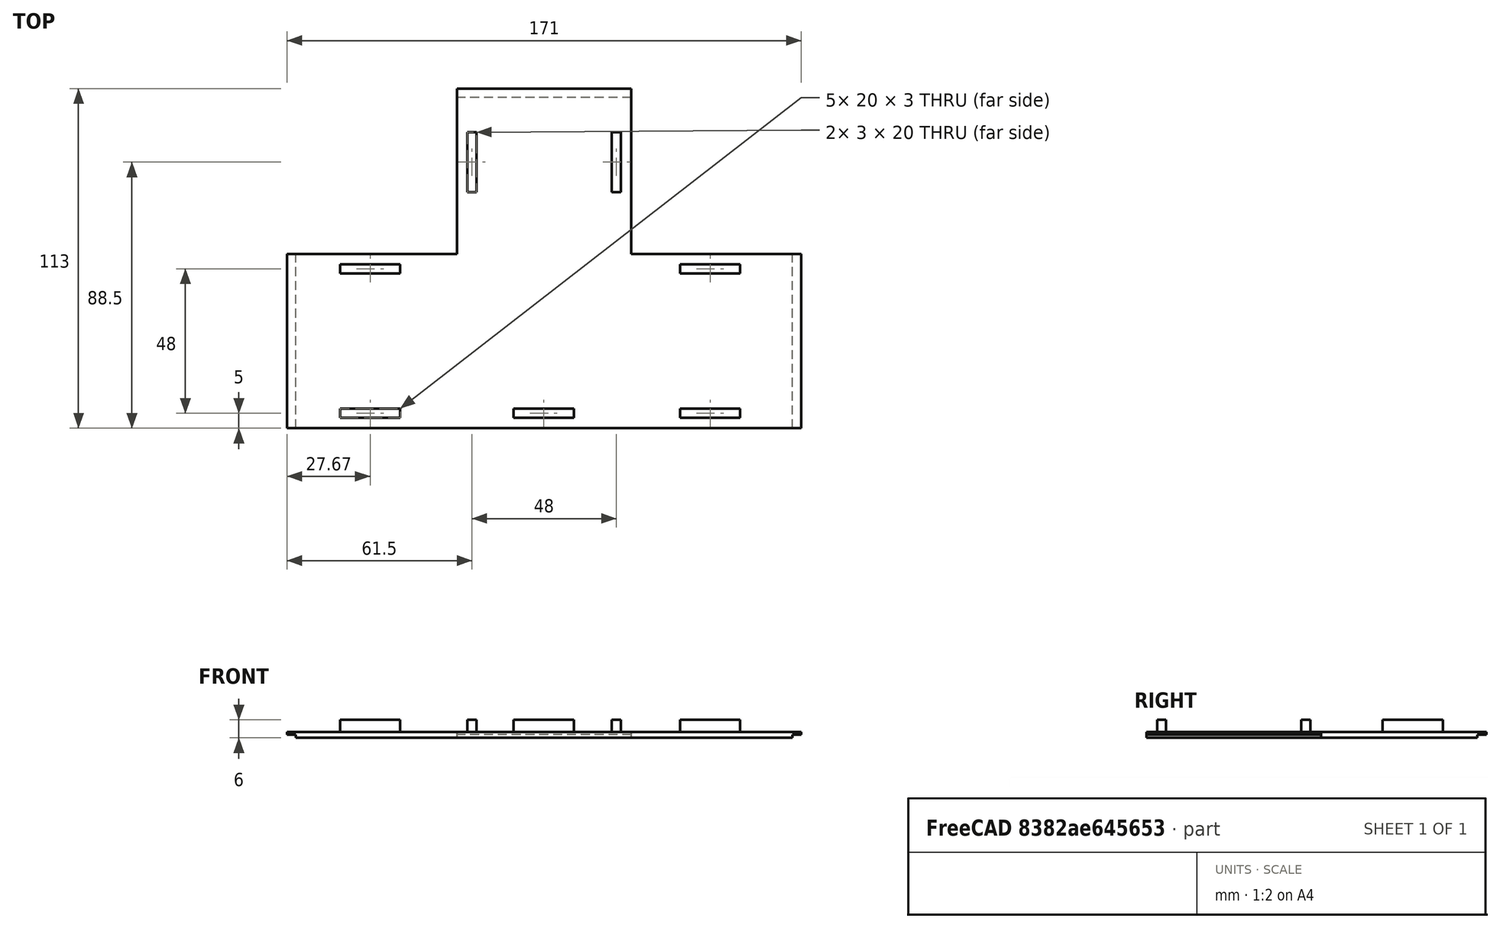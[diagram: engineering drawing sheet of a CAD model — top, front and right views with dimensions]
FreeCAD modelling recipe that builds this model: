
FCSTD DOCUMENT  (FreeCAD 0.21R33694 (Git))
Label: maze_cover_B
License: All rights reserved
LicenseURL: https://en.wikipedia.org/wiki/All_rights_reserved
objects: Part::Box×12, Part::MultiFuse×1
note: 13 computed .brp shape members not serialized (recipe doc carries the construction recipe); baked Part::Feature solids carry a one-line shape summary decoded from their .brp

FEATURE [Part::Box] Box  label="Cube"
  AttacherType = Attacher::AttachEngine3D
  Height = 2
  Length = 165
  Placement = pos=(4,0,0) rot=(0,0,1;0rad)
  Width = 58
FEATURE [Part::Box] Box001  label="Cube001"
  AttacherType = Attacher::AttachEngine3D
  Height = 2
  Length = 110
  Placement = pos=(115.5,0,0) rot=(0,0,1;1.5708rad)
  Width = 58
FEATURE [Part::Box] Box002  label="Cube002"
  AttacherType = Attacher::AttachEngine3D
  Height = 6
  Length = 20
  Placement = pos=(18.67,3.5,0) rot=(0,0,1;0rad)
  Width = 3
FEATURE [Part::Box] Box003  label="Cube003"
  AttacherType = Attacher::AttachEngine3D
  Height = 6
  Length = 20
  Placement = pos=(76.34,3.5,0) rot=(0,0,1;0rad)
  Width = 3
FEATURE [Part::Box] Box004  label="Cube004"
  AttacherType = Attacher::AttachEngine3D
  Height = 6
  Length = 20
  Placement = pos=(131.67,3.5,0) rot=(0,0,1;0rad)
  Width = 3
FEATURE [Part::Box] Box005  label="Cube005"
  AttacherType = Attacher::AttachEngine3D
  Height = 6
  Length = 20
  Placement = pos=(18.67,51.5,0) rot=(0,0,1;0rad)
  Width = 3
FEATURE [Part::Box] Box006  label="Cube006"
  AttacherType = Attacher::AttachEngine3D
  Height = 6
  Length = 20
  Placement = pos=(131.67,51.5,0) rot=(0,0,1;0rad)
  Width = 3
FEATURE [Part::Box] Box007  label="Cube007"
  AttacherType = Attacher::AttachEngine3D
  Height = 6
  Length = 20
  Placement = pos=(64,78.5,0) rot=(0,0,1;1.5708rad)
  Width = 3
FEATURE [Part::Box] Box008  label="Cube008"
  AttacherType = Attacher::AttachEngine3D
  Height = 6
  Length = 20
  Placement = pos=(112,78.5,0) rot=(0,0,1;1.5708rad)
  Width = 3
FEATURE [Part::Box] Box009  label="Cube009"
  AttacherType = Attacher::AttachEngine3D
  Height = 1
  Length = 3
  Placement = pos=(1,0,1) rot=(0,0,1;0rad)
  Width = 58
FEATURE [Part::Box] Box010  label="Cube010"
  AttacherType = Attacher::AttachEngine3D
  Height = 1
  Length = 3
  Placement = pos=(169,0,1) rot=(0,0,1;0rad)
  Width = 58
FEATURE [Part::Box] Box011  label="Cube011"
  AttacherType = Attacher::AttachEngine3D
  Height = 1
  Length = 3
  Placement = pos=(115.5,110,1) rot=(0,0,1;1.5708rad)
  Width = 58
FEATURE [Part::MultiFuse] Fusion
  Shapes = -> [Box011,Box010,Box009,Box008,Box007,Box006,Box005,Box004,Box003,Box002,Box001,Box]
